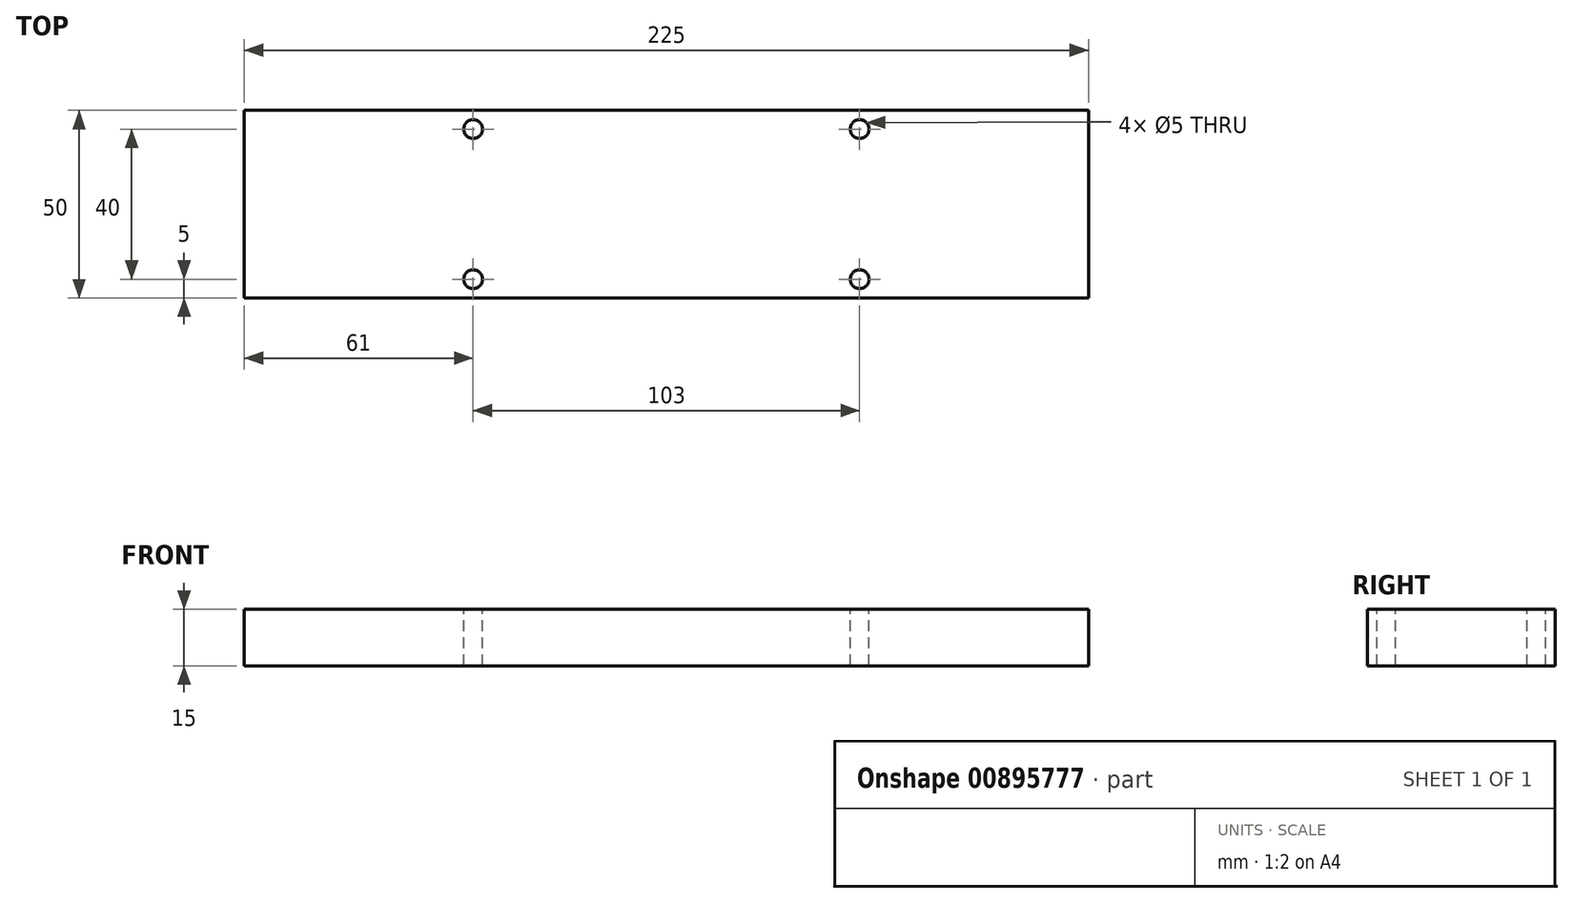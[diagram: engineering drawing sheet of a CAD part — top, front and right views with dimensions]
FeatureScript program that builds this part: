
annotation { "Feature Type Name" : "Feature", "Feature Type Description" : "" }
export const myFeature = defineFeature(function(context is Context, id is Id, definition is map)
    precondition{}
    {
        {
            var Q0;
            Q0=qCreatedBy(makeId("Front.planeOp"),FACE);
            var sketch = newSketch(context, id + "F0", { "sketchPlane" : qUnion([Q0])});
            skLineSegment(sketch, "E0.bottom", {"start": v(-112.5, 7.5) * mm, "end": v(112.5, 7.5) * mm});
            skLineSegment(sketch, "E0.top", {"start": v(-112.5, -7.5) * mm, "end": v(112.5, -7.5) * mm});
            skLineSegment(sketch, "E0.left", {"start": v(-112.5, 7.5) * mm, "end": v(-112.5, -7.5) * mm});
            skLineSegment(sketch, "E0.right", {"start": v(112.5, 7.5) * mm, "end": v(112.5, -7.5) * mm});
            skPoint(sketch, "E0.middle", {"position": v(0, 0) * mm});
            skSolve(sketch);
        }
        {
            var Q0;
            Q0 = qSketchRegion(id + "F0", true);
            extrude(context, id + "F1", {"entities" : qUnion([Q0]), "depth" : 50 * mm, "offsetDistance" : 25 * mm});
        }
        {
            var Q0;
            Q0=makeQuery(id+"F1.opExtrude","SWEPT_FACE",FACE,{"disambiguationData":[OSD([sQuery(id+"F0.wireOp",EDGE,"E0.bottom")])]});
            var sketch = newSketch(context, id + "F2", { "sketchPlane" : qUnion([Q0])});
            skCircle(sketch, "E1", {"center": v(-51.5, -5) * mm, "radius": 2.5 * mm});
            skCircle(sketch, "E2.MirrorC", {"center": v(51.5, -5) * mm, "radius": 2.5 * mm});
            skCircle(sketch, "E3", {"center": v(-51.5, -45) * mm, "radius": 2.5 * mm});
            skCircle(sketch, "E4.MirrorC", {"center": v(51.5, -45) * mm, "radius": 2.5 * mm});
            skSolve(sketch);
        }
        {
            var Q0;
            Q0 = qSketchRegion(id + "F2", true);
            extrude(context, id + "F3", {"entities" : qUnion([Q0]), "operationType" : NewBodyOperationType.REMOVE, "endBound" : BoundingType.THROUGH_ALL, "oppositeDirection" : true, "depth" : 25 * mm, "offsetDistance" : 25 * mm});
        }
    });
